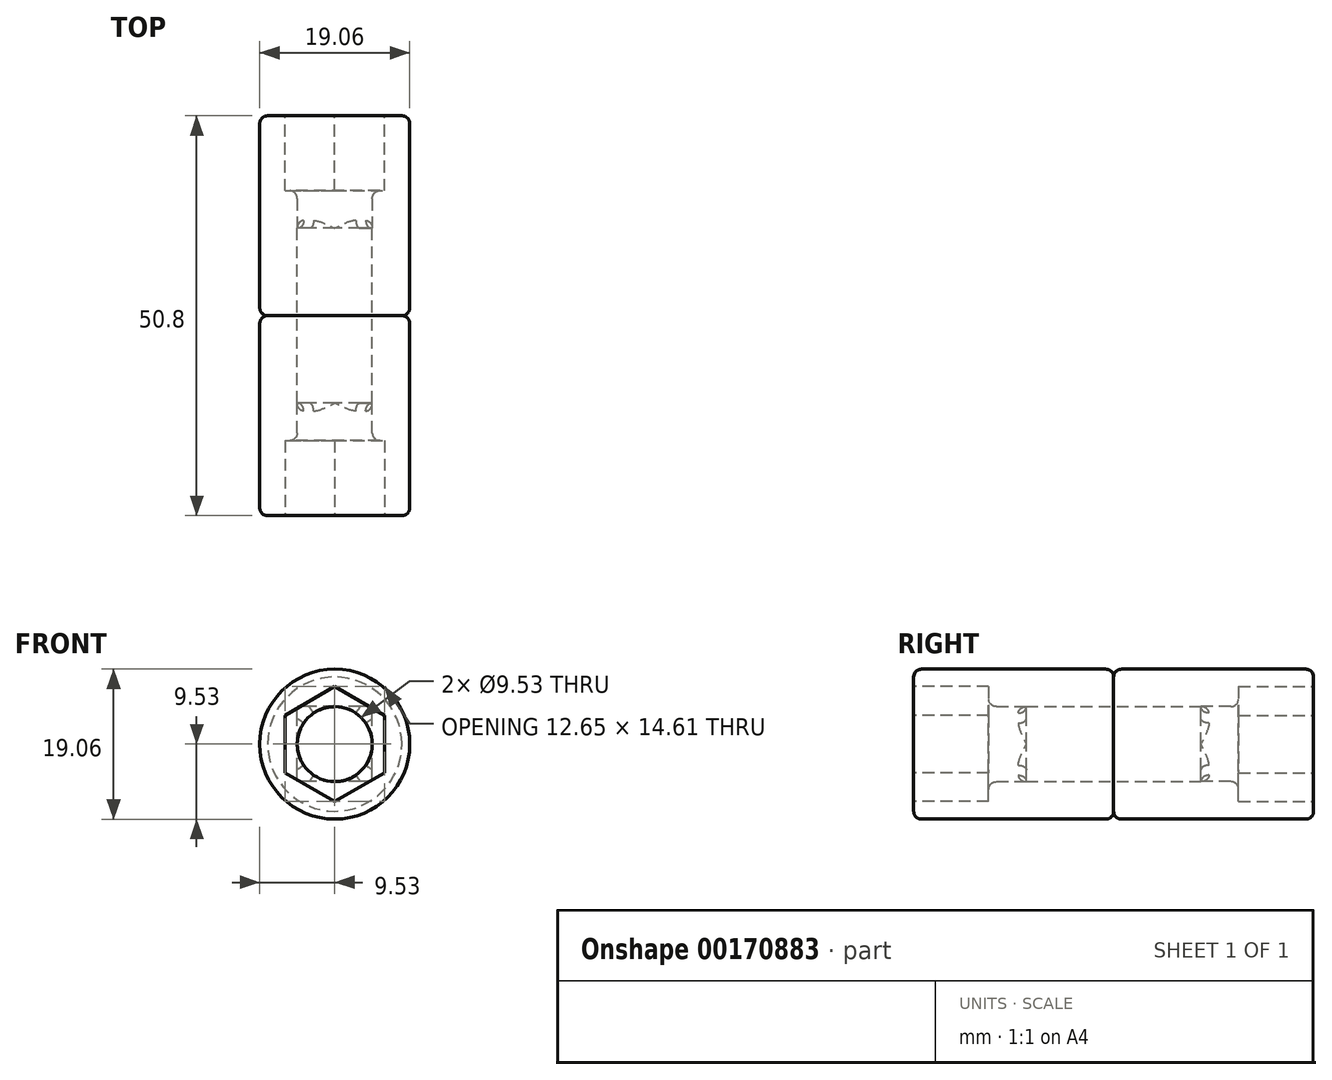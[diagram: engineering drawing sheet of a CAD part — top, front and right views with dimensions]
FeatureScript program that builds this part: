
annotation { "Feature Type Name" : "Feature", "Feature Type Description" : "" }
export const myFeature = defineFeature(function(context is Context, id is Id, definition is map)
    precondition{}
    {
        {
            var Q0;
            Q0=qCreatedBy(makeId("Front.planeOp"),FACE);
            var sketch = newSketch(context, id + "F0", { "sketchPlane" : qUnion([Q0])});
            skCircle(sketch, "E0", {"center": v(0, 0) * mm, "radius": 9.53 * mm});
            skSolve(sketch);
        }
        {
            var Q0;
            Q0 = qSketchRegion(id + "F0", true);
            extrude(context, id + "F1", {"entities" : qUnion([Q0]), "depth" : 25.4 * mm});
        }
        {
            var Q0;
            Q0=qCreatedBy(makeId("Front.planeOp"),FACE);
            var sketch = newSketch(context, id + "F2", { "sketchPlane" : qUnion([Q0])});
            skLineSegment(sketch, "E1.bottom", {"start": v(4.76, 4.76) * mm, "end": v(-4.76, 4.76) * mm});
            skLineSegment(sketch, "E1.top", {"start": v(4.76, -4.76) * mm, "end": v(-4.76, -4.76) * mm});
            skLineSegment(sketch, "E1.left", {"start": v(4.76, -4.76) * mm, "end": v(4.76, 4.76) * mm});
            skLineSegment(sketch, "E1.right", {"start": v(-4.76, -4.76) * mm, "end": v(-4.76, 4.76) * mm});
            skPoint(sketch, "E1.middle", {"position": v(0, 0) * mm});
            skCircle(sketch, "E2", {"center": v(0, 0) * mm, "radius": 4.76 * mm});
            skSolve(sketch);
        }
        {
            var Q0;
            {var subQ0=sQuery(id+"F2.wireOp",EDGE,"E2");var subQ1=makeQuery(id+"F2.imprint","INTERSECT",VERTEX,{"derivedFrom":[sQuery(id+"F2.wireOp",EDGE,"E1.bottom"),subQ0]});Q0=makeQuery(id+"F2.imprint","IMPRINT",FACE,{"disambiguationData":[TD([[makeQuery(id+"F2.imprint","IMPRINT",EDGE,{"disambiguationData":[TD([[subQ1,1.0]])],"derivedFrom":subQ0}),1.0]])]});}
            extrude(context, id + "F3", {"entities" : qUnion([Q0]), "operationType" : NewBodyOperationType.REMOVE, "endBound" : BoundingType.THROUGH_ALL, "depth" : 25.4 * mm});
        }
        {
            var Q0;
            Q0 = qSketchRegion(id + "F2", true);
            extrude(context, id + "F4", {"entities" : qUnion([Q0]), "operationType" : NewBodyOperationType.REMOVE, "depth" : 11.1 * mm});
        }
        {
            var Q0;
            Q0=makeQuery(id+"F1.opExtrude","CAP_FACE",FACE,{"disambiguationData":[OSD([sQuery(id+"F0.wireOp",EDGE,"E0")])],"isStart":false});
            var sketch = newSketch(context, id + "F5", { "sketchPlane" : qUnion([Q0])});
            skCircle(sketch, "E3.cCircle", {"center": v(0, 0) * mm, "radius": 6.32 * mm, "construction": true});
            skLineSegment(sketch, "E3.0", {"start": v(6.32, 3.65) * mm, "end": v(6.32, -3.65) * mm});
            skLineSegment(sketch, "E3.1", {"start": v(6.32, -3.65) * mm, "end": v(0, -7.3) * mm});
            skLineSegment(sketch, "E3.2", {"start": v(0, -7.3) * mm, "end": v(-6.32, -3.65) * mm});
            skLineSegment(sketch, "E3.3", {"start": v(-6.32, -3.65) * mm, "end": v(-6.32, 3.65) * mm});
            skLineSegment(sketch, "E3.4", {"start": v(-6.32, 3.65) * mm, "end": v(0, 7.3) * mm});
            skLineSegment(sketch, "E3.5", {"start": v(0, 7.3) * mm, "end": v(6.32, 3.65) * mm});
            skPoint(sketch, "E3.0.midPoint", {"position": v(6.32, 0) * mm});
            skSolve(sketch);
        }
        {
            var Q0;
            Q0 = qSketchRegion(id + "F5", true);
            extrude(context, id + "F6", {"entities" : qUnion([Q0]), "operationType" : NewBodyOperationType.REMOVE, "oppositeDirection" : true, "depth" : 9.52 * mm});
        }
        {
            var Q0;
            Q0=makeQuery(id+"F1.opExtrude","CAP_EDGE",EDGE,{"disambiguationData":[OSD([sQuery(id+"F0.wireOp",EDGE,"E0")])],"isStart":true});
            var Q1;
            Q1=makeQuery(id+"F1.opExtrude","CAP_EDGE",EDGE,{"disambiguationData":[OSD([sQuery(id+"F0.wireOp",EDGE,"E0")])],"isStart":false});
            var Q2;
            Q2=makeQuery(id+"F6.boolean.opBoolean","COPY",EDGE,{"derivedFrom":makeQuery(id+"F6.opExtrude","CAP_EDGE",EDGE,{"disambiguationData":[OSD([sQuery(id+"F5.wireOp",EDGE,"E3.2")])],"isStart":true})});
            var Q3;
            Q3=makeQuery(id+"F6.boolean.opBoolean","COPY",EDGE,{"derivedFrom":makeQuery(id+"F6.opExtrude","CAP_EDGE",EDGE,{"disambiguationData":[OSD([sQuery(id+"F5.wireOp",EDGE,"E3.3")])],"isStart":true})});
            var Q4;
            Q4=makeQuery(id+"F6.boolean.opBoolean","COPY",EDGE,{"derivedFrom":makeQuery(id+"F6.opExtrude","CAP_EDGE",EDGE,{"disambiguationData":[OSD([sQuery(id+"F5.wireOp",EDGE,"E3.4")])],"isStart":true})});
            var Q5;
            Q5=makeQuery(id+"F6.boolean.opBoolean","COPY",EDGE,{"derivedFrom":makeQuery(id+"F6.opExtrude","CAP_EDGE",EDGE,{"disambiguationData":[OSD([sQuery(id+"F5.wireOp",EDGE,"E3.5")])],"isStart":true})});
            var Q6;
            Q6=makeQuery(id+"F6.boolean.opBoolean","COPY",EDGE,{"derivedFrom":makeQuery(id+"F6.opExtrude","CAP_EDGE",EDGE,{"disambiguationData":[OSD([sQuery(id+"F5.wireOp",EDGE,"E3.0")])],"isStart":true})});
            var Q7;
            Q7=makeQuery(id+"F6.boolean.opBoolean","COPY",EDGE,{"derivedFrom":makeQuery(id+"F6.opExtrude","CAP_EDGE",EDGE,{"disambiguationData":[OSD([sQuery(id+"F5.wireOp",EDGE,"E3.1")])],"isStart":true})});
            var Q8;
            Q8=makeQuery(id+"F4.boolean.opBoolean","COPY",EDGE,{"derivedFrom":makeQuery(id+"F4.opExtrude","CAP_EDGE",EDGE,{"disambiguationData":[OSD([sQuery(id+"F2.wireOp",EDGE,"E1.right")])],"isStart":true})});
            var Q9;
            Q9=makeQuery(id+"F4.boolean.opBoolean","COPY",EDGE,{"derivedFrom":makeQuery(id+"F4.opExtrude","CAP_EDGE",EDGE,{"disambiguationData":[OSD([sQuery(id+"F2.wireOp",EDGE,"E1.top")])],"isStart":true})});
            var Q10;
            Q10=makeQuery(id+"F4.boolean.opBoolean","COPY",EDGE,{"derivedFrom":makeQuery(id+"F4.opExtrude","CAP_EDGE",EDGE,{"disambiguationData":[OSD([sQuery(id+"F2.wireOp",EDGE,"E1.left")])],"isStart":true})});
            var Q11;
            Q11=makeQuery(id+"F4.boolean.opBoolean","COPY",EDGE,{"derivedFrom":makeQuery(id+"F4.opExtrude","CAP_EDGE",EDGE,{"disambiguationData":[OSD([sQuery(id+"F2.wireOp",EDGE,"E1.bottom")])],"isStart":true})});
            var Q12;
            Q12=makeQuery(id+"F4.boolean.opBoolean","INTERSECT",EDGE,{"disambiguationData":[OD(2.0)],"derivedFrom":[makeQuery(id+"F3.boolean.opBoolean","COPY",FACE,{"derivedFrom":makeQuery(id+"F3.opExtrude","SWEPT_FACE",FACE,{"disambiguationData":[OSD([sQuery(id+"F2.wireOp",EDGE,"E2")])]})}),makeQuery(id+"F4.opExtrude","CAP_FACE",FACE,{"disambiguationData":[OSD([sQuery(id+"F2.wireOp",EDGE,"E1.bottom"),sQuery(id+"F2.wireOp",EDGE,"E1.top"),sQuery(id+"F2.wireOp",EDGE,"E1.left"),sQuery(id+"F2.wireOp",EDGE,"E1.right")])],"isStart":false})]});
            var Q13;
            Q13=makeQuery(id+"F6.boolean.opBoolean","INTERSECT",EDGE,{"derivedFrom":[makeQuery(id+"F3.boolean.opBoolean","COPY",FACE,{"derivedFrom":makeQuery(id+"F3.opExtrude","SWEPT_FACE",FACE,{"disambiguationData":[OSD([sQuery(id+"F2.wireOp",EDGE,"E2")])]})}),makeQuery(id+"F6.opExtrude","CAP_FACE",FACE,{"disambiguationData":[OSD([sQuery(id+"F5.wireOp",EDGE,"E3.0"),sQuery(id+"F5.wireOp",EDGE,"E3.1"),sQuery(id+"F5.wireOp",EDGE,"E3.2"),sQuery(id+"F5.wireOp",EDGE,"E3.3"),sQuery(id+"F5.wireOp",EDGE,"E3.4"),sQuery(id+"F5.wireOp",EDGE,"E3.5")])],"isStart":false})]});
            fillet(context, id + "F7", {"entities" : qUnion([Q0, Q1, Q2, Q3, Q4, Q5, Q6, Q7, Q8, Q9, Q10, Q11, Q12, Q13]), "radius" : 1 * mm, "tangentPropagation" : true, "allowEdgeOverflow" : false});
        }
        {
            var Q0;
            Q0=makeQuery(id+"F1.opExtrude","SWEPT_BODY",BODY,{"disambiguationData":[OSD([sQuery(id+"F0.wireOp",EDGE,"E0")])]});
            var Q1;
            Q1=qCreatedBy(makeId("Front.planeOp"),FACE);
            mirror(context, id + "F8", {"operationType" : NewBodyOperationType.ADD, "entities" : qUnion([Q0]), "mirrorPlane" : qUnion([Q1])});
        }
    });
